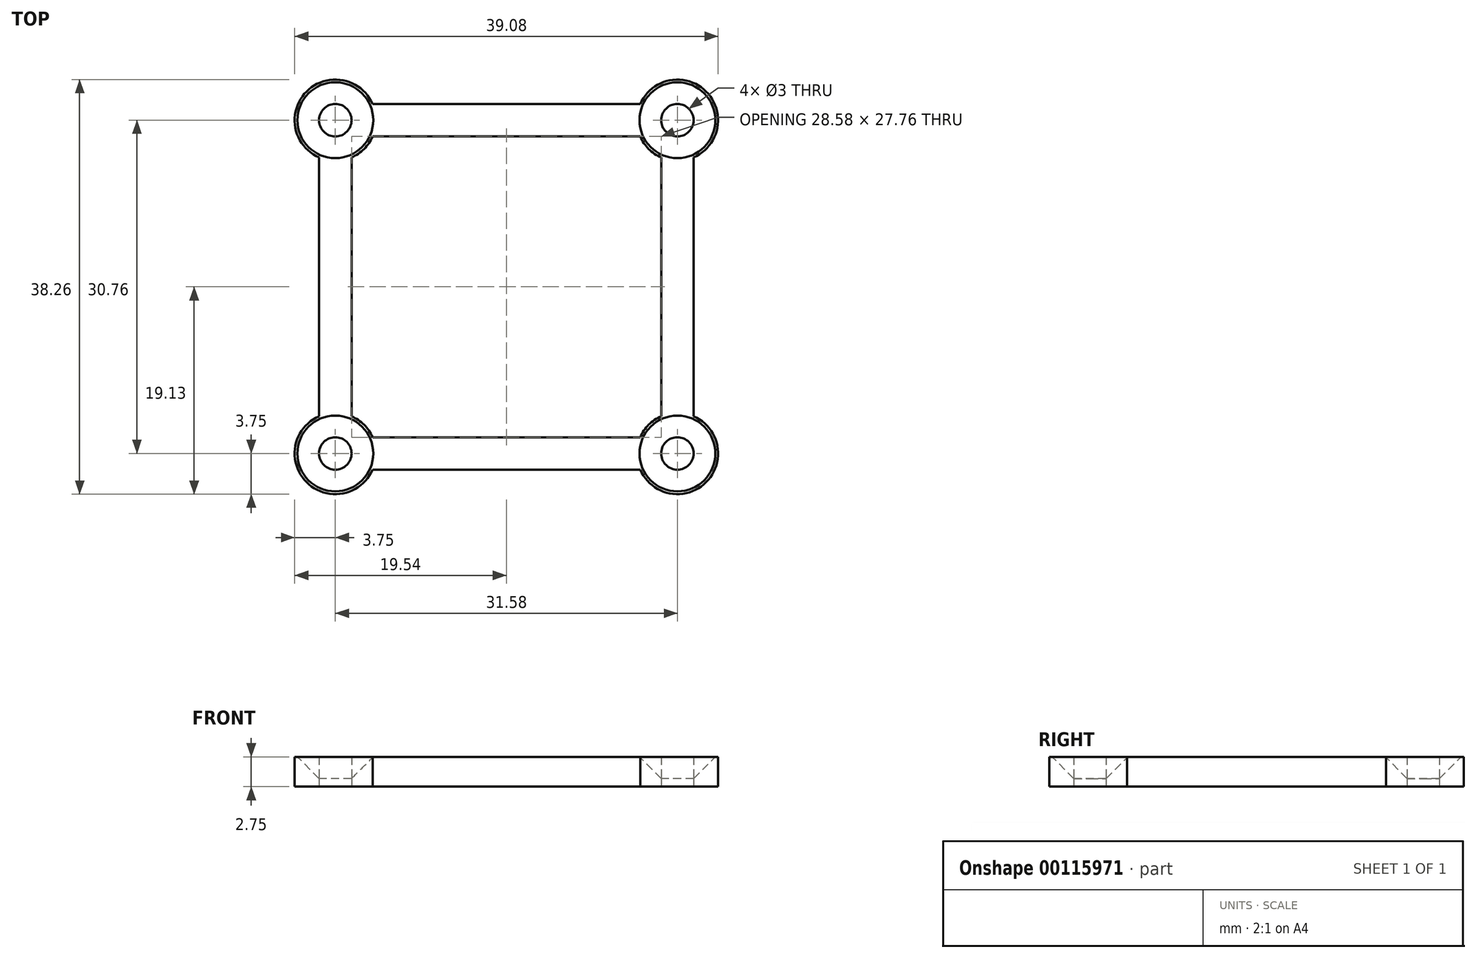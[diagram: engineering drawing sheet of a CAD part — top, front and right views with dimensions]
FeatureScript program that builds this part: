
annotation { "Feature Type Name" : "Feature", "Feature Type Description" : "" }
export const myFeature = defineFeature(function(context is Context, id is Id, definition is map)
    precondition{}
    {
        {
            var Q0;
            Q0=qCreatedBy(makeId("Top.planeOp"),FACE);
            var sketch = newSketch(context, id + "F0", { "sketchPlane" : qUnion([Q0])});
            skLineSegment(sketch, "E0.bottom", {"start": v(20.9, -22.88) * mm, "end": v(-20.9, -22.88) * mm, "construction": true});
            skLineSegment(sketch, "E0.top", {"start": v(20.9, 22.88) * mm, "end": v(-20.9, 22.88) * mm, "construction": true});
            skLineSegment(sketch, "E0.left", {"start": v(20.9, -22.88) * mm, "end": v(20.9, 22.88) * mm, "construction": true});
            skLineSegment(sketch, "E0.right", {"start": v(-20.9, -22.88) * mm, "end": v(-20.9, 22.88) * mm, "construction": true});
            skPoint(sketch, "E0.middle", {"position": v(0, 0) * mm});
            skCircle(sketch, "E1", {"center": v(-15.79, 15.38) * mm, "radius": 1.5 * mm});
            skCircle(sketch, "E2", {"center": v(15.79, 15.38) * mm, "radius": 1.5 * mm});
            skCircle(sketch, "E3", {"center": v(-15.79, -15.38) * mm, "radius": 1.5 * mm});
            skCircle(sketch, "E4", {"center": v(15.8, -15.38) * mm, "radius": 1.5 * mm});
            skLineSegment(sketch, "E5", {"start": v(-15.8, 15.38) * mm, "end": v(-15.8, 22.88) * mm, "construction": true});
            skLineSegment(sketch, "E6", {"start": v(-15.8, 15.38) * mm, "end": v(-15.79, -15.38) * mm, "construction": true});
            skLineSegment(sketch, "E7", {"start": v(-15.79, -15.38) * mm, "end": v(-15.79, -22.88) * mm, "construction": true});
            skLineSegment(sketch, "E8", {"start": v(-15.79, -15.38) * mm, "end": v(15.8, -15.38) * mm, "construction": true});
            skLineSegment(sketch, "E9", {"start": v(15.8, -15.38) * mm, "end": v(15.8, 15.38) * mm, "construction": true});
            skLineSegment(sketch, "E10", {"start": v(15.79, 15.38) * mm, "end": v(-15.79, 15.38) * mm, "construction": true});
            skLineSegment(sketch, "E11", {"start": v(-15.79, 15.38) * mm, "end": v(-20.9, 15.38) * mm, "construction": true});
            skLineSegment(sketch, "E12", {"start": v(15.8, 15.38) * mm, "end": v(15.8, 22.88) * mm, "construction": true});
            skLineSegment(sketch, "E13", {"start": v(-15.79, -15.38) * mm, "end": v(-20.89, -15.38) * mm, "construction": true});
            skLineSegment(sketch, "E14", {"start": v(15.8, -15.38) * mm, "end": v(15.8, -22.88) * mm, "construction": true});
            skLineSegment(sketch, "E15", {"start": v(15.8, -15.38) * mm, "end": v(20.9, -15.38) * mm, "construction": true});
            skLineSegment(sketch, "E16", {"start": v(15.79, 15.38) * mm, "end": v(20.9, 15.38) * mm, "construction": true});
            skCircle(sketch, "E17", {"center": v(-15.79, 15.38) * mm, "radius": 3.75 * mm});
            skCircle(sketch, "E18", {"center": v(15.79, 15.38) * mm, "radius": 3.75 * mm});
            skCircle(sketch, "E19", {"center": v(15.8, -15.38) * mm, "radius": 3.75 * mm});
            skCircle(sketch, "E20", {"center": v(-15.79, -15.38) * mm, "radius": 3.75 * mm});
            skLineSegment(sketch, "E21.bottom", {"start": v(-17.29, 15.38) * mm, "end": v(-14.29, 15.38) * mm});
            skLineSegment(sketch, "E21.top", {"start": v(-17.29, -15.38) * mm, "end": v(-14.29, -15.38) * mm});
            skLineSegment(sketch, "E21.left", {"start": v(-17.29, 15.38) * mm, "end": v(-17.29, -15.38) * mm});
            skLineSegment(sketch, "E21.right", {"start": v(-14.29, 15.38) * mm, "end": v(-14.29, -15.38) * mm});
            skLineSegment(sketch, "E22.bottom", {"start": v(-15.79, -13.88) * mm, "end": v(15.8, -13.88) * mm});
            skLineSegment(sketch, "E22.top", {"start": v(-15.79, -16.88) * mm, "end": v(15.8, -16.88) * mm});
            skLineSegment(sketch, "E22.left", {"start": v(-15.79, -13.88) * mm, "end": v(-15.79, -16.88) * mm});
            skLineSegment(sketch, "E22.right", {"start": v(15.8, -13.88) * mm, "end": v(15.8, -16.88) * mm});
            skLineSegment(sketch, "E23.bottom", {"start": v(14.29, 15.38) * mm, "end": v(17.3, 15.38) * mm});
            skLineSegment(sketch, "E23.top", {"start": v(14.29, -15.38) * mm, "end": v(17.3, -15.38) * mm});
            skLineSegment(sketch, "E23.left", {"start": v(14.29, 15.38) * mm, "end": v(14.29, -15.38) * mm});
            skLineSegment(sketch, "E23.right", {"start": v(17.3, 15.38) * mm, "end": v(17.3, -15.38) * mm});
            skLineSegment(sketch, "E24.bottom", {"start": v(15.8, 16.88) * mm, "end": v(-15.8, 16.88) * mm});
            skLineSegment(sketch, "E24.top", {"start": v(15.8, 13.88) * mm, "end": v(-15.8, 13.88) * mm});
            skLineSegment(sketch, "E24.left", {"start": v(15.8, 16.88) * mm, "end": v(15.8, 13.88) * mm});
            skLineSegment(sketch, "E24.right", {"start": v(-15.8, 16.88) * mm, "end": v(-15.8, 13.88) * mm});
            skSolve(sketch);
        }
        {
            var Q0;
            Q0 = qSketchRegion(id + "F0", true);
            var Q1;
            {var subQ0=sQuery(id+"F0.wireOp",EDGE,"E21.right");var subQ3=sQuery(id+"F0.wireOp",EDGE,"E24.top");var subQ5=makeQuery(id+"F0.imprint","INTERSECT",VERTEX,{"derivedFrom":[subQ0,subQ3]});Q1=makeQuery(id+"F0.imprint","IMPRINT",FACE,{"disambiguationData":[TD([[makeQuery(id+"F0.imprint","IMPRINT",EDGE,{"disambiguationData":[TD([[subQ5,1.0]])],"derivedFrom":subQ0}),-1.0]])]});}
            var Q2;
            {var subQ0=sQuery(id+"F0.wireOp",EDGE,"E21.right");var subQ1=sQuery(id+"F0.wireOp",EDGE,"E17");var subQ2=makeQuery(id+"F0.imprint","INTERSECT",VERTEX,{"derivedFrom":[subQ1,subQ0]});Q2=makeQuery(id+"F0.imprint","IMPRINT",FACE,{"disambiguationData":[TD([[makeQuery(id+"F0.imprint","IMPRINT",EDGE,{"disambiguationData":[TD([[subQ2,-1.0]])],"derivedFrom":subQ1}),1.0]])]});}
            var Q3;
            {var subQ0=sQuery(id+"F0.wireOp",EDGE,"E24.top");var subQ1=sQuery(id+"F0.wireOp",EDGE,"E18");var subQ2=makeQuery(id+"F0.imprint","INTERSECT",VERTEX,{"derivedFrom":[subQ1,subQ0]});Q3=makeQuery(id+"F0.imprint","IMPRINT",FACE,{"disambiguationData":[TD([[makeQuery(id+"F0.imprint","IMPRINT",EDGE,{"disambiguationData":[TD([[subQ2,-1.0]])],"derivedFrom":subQ1}),1.0]])]});}
            var Q4;
            {var subQ0=sQuery(id+"F0.wireOp",EDGE,"E23.left");var subQ3=sQuery(id+"F0.wireOp",EDGE,"E24.top");var subQ5=makeQuery(id+"F0.imprint","INTERSECT",VERTEX,{"derivedFrom":[subQ0,subQ3]});Q4=makeQuery(id+"F0.imprint","IMPRINT",FACE,{"disambiguationData":[TD([[makeQuery(id+"F0.imprint","IMPRINT",EDGE,{"disambiguationData":[TD([[subQ5,1.0]])],"derivedFrom":subQ0}),1.0]])]});}
            var Q5;
            {var subQ0=sQuery(id+"F0.wireOp",EDGE,"E21.right");var subQ3=sQuery(id+"F0.wireOp",EDGE,"E22.bottom");var subQ5=makeQuery(id+"F0.imprint","INTERSECT",VERTEX,{"derivedFrom":[subQ0,subQ3]});Q5=makeQuery(id+"F0.imprint","IMPRINT",FACE,{"disambiguationData":[TD([[makeQuery(id+"F0.imprint","IMPRINT",EDGE,{"disambiguationData":[TD([[subQ5,-1.0]])],"derivedFrom":subQ0}),-1.0]])]});}
            var Q6;
            {var subQ0=sQuery(id+"F0.wireOp",EDGE,"E21.right");var subQ1=sQuery(id+"F0.wireOp",EDGE,"E20");var subQ2=makeQuery(id+"F0.imprint","INTERSECT",VERTEX,{"derivedFrom":[subQ1,subQ0]});Q6=makeQuery(id+"F0.imprint","IMPRINT",FACE,{"disambiguationData":[TD([[makeQuery(id+"F0.imprint","IMPRINT",EDGE,{"disambiguationData":[TD([[subQ2,1.0]])],"derivedFrom":subQ1}),1.0]])]});}
            var Q7;
            {var subQ0=sQuery(id+"F0.wireOp",EDGE,"E22.bottom");var subQ3=sQuery(id+"F0.wireOp",EDGE,"E23.left");var subQ5=makeQuery(id+"F0.imprint","INTERSECT",VERTEX,{"derivedFrom":[subQ0,subQ3]});Q7=makeQuery(id+"F0.imprint","IMPRINT",FACE,{"disambiguationData":[TD([[makeQuery(id+"F0.imprint","IMPRINT",EDGE,{"disambiguationData":[TD([[subQ5,-1.0]])],"derivedFrom":subQ0}),-1.0]])]});}
            var Q8;
            {var subQ0=sQuery(id+"F0.wireOp",EDGE,"E23.left");var subQ1=sQuery(id+"F0.wireOp",EDGE,"E19");var subQ2=makeQuery(id+"F0.imprint","INTERSECT",VERTEX,{"derivedFrom":[subQ1,subQ0]});Q8=makeQuery(id+"F0.imprint","IMPRINT",FACE,{"disambiguationData":[TD([[makeQuery(id+"F0.imprint","IMPRINT",EDGE,{"disambiguationData":[TD([[subQ2,-1.0]])],"derivedFrom":subQ1}),1.0]])]});}
            extrude(context, id + "F1", {"entities" : qUnion([Q0, Q1, Q2, Q3, Q4, Q5, Q6, Q7, Q8]), "depth" : 2.75 * mm});
        }
        {
            var Q0;
            Q0=makeQuery(id+"F1.opExtrude","CAP_EDGE",EDGE,{"disambiguationData":[OSD([sQuery(id+"F0.wireOp",EDGE,"E1")])],"isStart":false});
            var Q1;
            Q1=makeQuery(id+"F1.opExtrude","CAP_EDGE",EDGE,{"disambiguationData":[OSD([sQuery(id+"F0.wireOp",EDGE,"E2")])],"isStart":false});
            var Q2;
            Q2=makeQuery(id+"F1.opExtrude","CAP_EDGE",EDGE,{"disambiguationData":[OSD([sQuery(id+"F0.wireOp",EDGE,"E4")])],"isStart":false});
            var Q3;
            Q3=makeQuery(id+"F1.opExtrude","CAP_EDGE",EDGE,{"disambiguationData":[OSD([sQuery(id+"F0.wireOp",EDGE,"E3")])],"isStart":false});
            chamfer(context, id + "F2", {"entities" : qUnion([Q0, Q1, Q2, Q3]), "chamferType" : ChamferType.OFFSET_ANGLE, "width" : 2 * mm, "oppositeDirection" : false, "angle" : 45 * degree, "tangentPropagation" : true});
        }
    });
